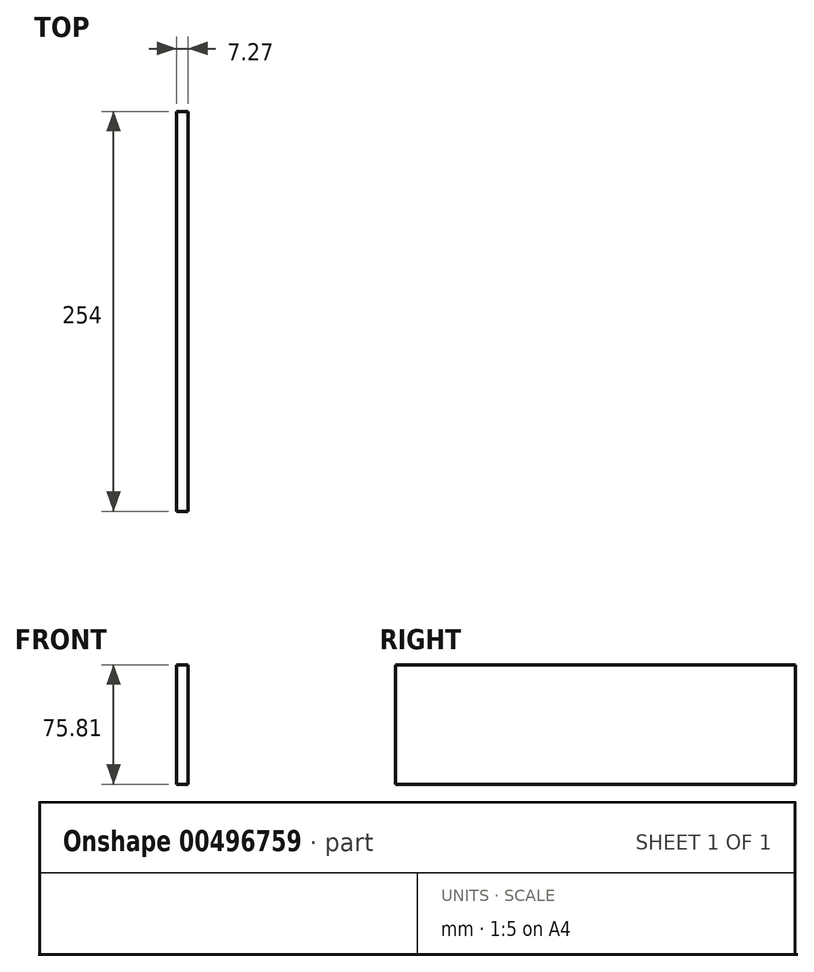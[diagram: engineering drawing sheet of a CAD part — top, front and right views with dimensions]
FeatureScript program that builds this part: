
annotation { "Feature Type Name" : "Feature", "Feature Type Description" : "" }
export const myFeature = defineFeature(function(context is Context, id is Id, definition is map)
    precondition{}
    {
        {
            var Q0;
            Q0=qCreatedBy(makeId("Front.planeOp"),FACE);
            var sketch = newSketch(context, id + "F0", { "sketchPlane" : qUnion([Q0])});
            skLineSegment(sketch, "E0", {"start": v(-76.37, 0) * mm, "end": v(-76.37, 75.81) * mm});
            skLineSegment(sketch, "E1", {"start": v(-76.37, 75.81) * mm, "end": v(-69.1, 75.81) * mm});
            skLineSegment(sketch, "E2", {"start": v(-69.1, 75.81) * mm, "end": v(-69.1, 0) * mm});
            skLineSegment(sketch, "E3", {"start": v(-69.1, 0) * mm, "end": v(-76.37, 0) * mm});
            skSolve(sketch);
        }
        {
            var Q0;
            Q0=makeQuery(id+"F0.imprint","IMPRINT",FACE,{"disambiguationData":[TD([[makeQuery(id+"F0.imprint","IMPRINT",EDGE,{"derivedFrom":sQuery(id+"F0.wireOp",EDGE,"E0")}),-1.0]])]});
            extrude(context, id + "F1", {"entities" : qUnion([Q0]), "depth" : 254 * mm});
        }
    });
